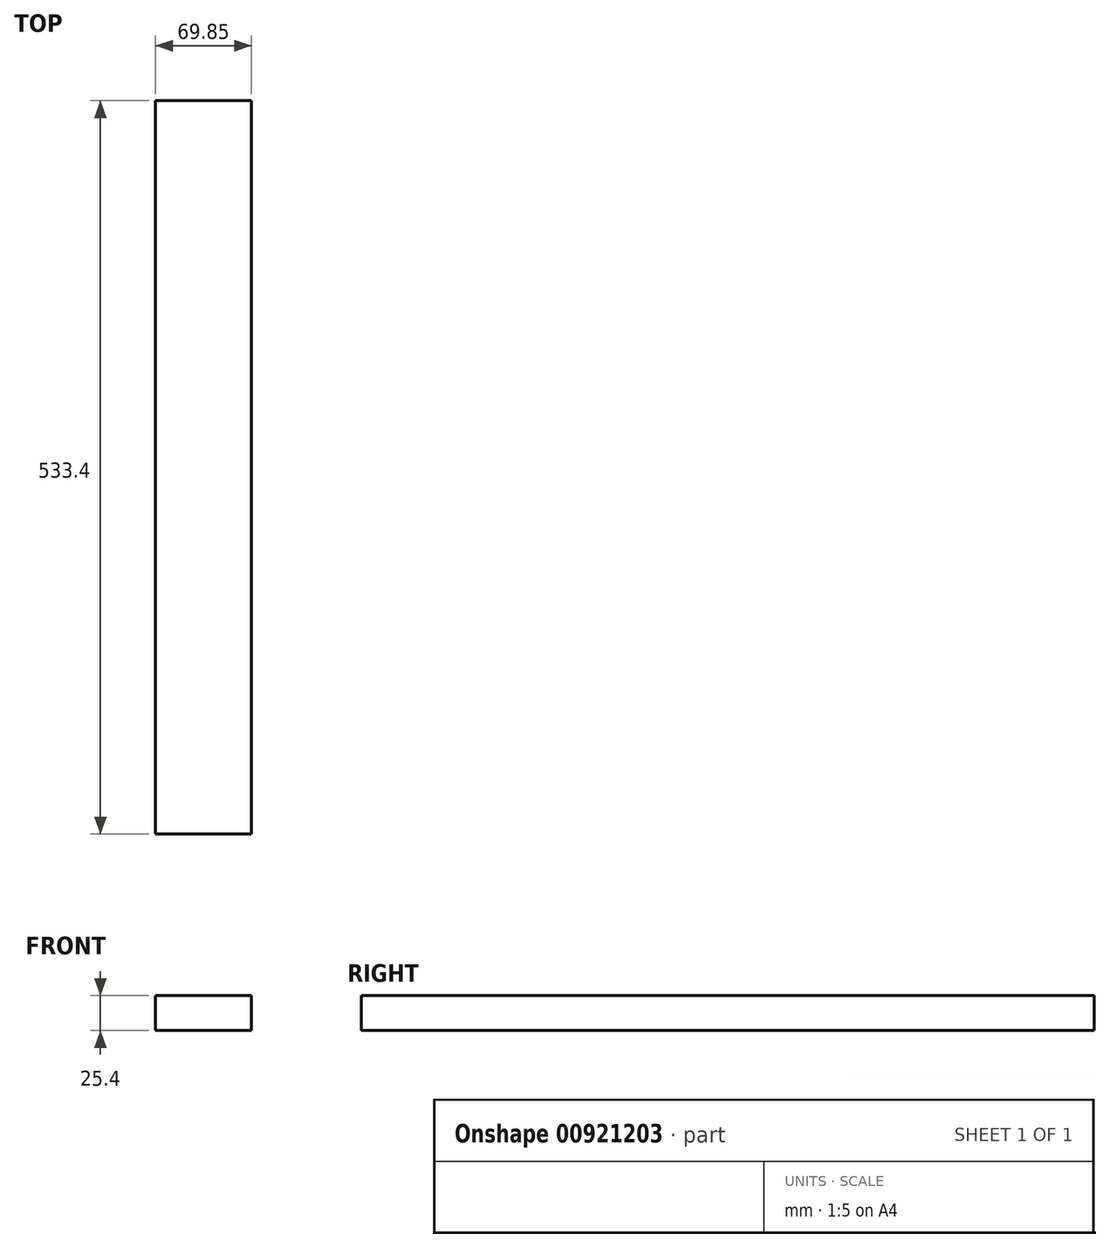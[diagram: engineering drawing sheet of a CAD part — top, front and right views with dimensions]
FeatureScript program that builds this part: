
annotation { "Feature Type Name" : "Feature", "Feature Type Description" : "" }
export const myFeature = defineFeature(function(context is Context, id is Id, definition is map)
    precondition{}
    {
        {
            var Q0;
            Q0=qCreatedBy(makeId("Front.planeOp"),FACE);
            var sketch = newSketch(context, id + "F0", { "sketchPlane" : qUnion([Q0])});
            skLineSegment(sketch, "E0.bottom", {"start": v(0, 0) * mm, "end": v(69.85, 0) * mm});
            skLineSegment(sketch, "E0.top", {"start": v(0, 25.4) * mm, "end": v(69.85, 25.4) * mm});
            skLineSegment(sketch, "E0.left", {"start": v(0, 0) * mm, "end": v(0, 25.4) * mm});
            skLineSegment(sketch, "E0.right", {"start": v(69.85, 0) * mm, "end": v(69.85, 25.4) * mm});
            skSolve(sketch);
        }
        {
            var Q0;
            Q0 = qSketchRegion(id + "F0", true);
            extrude(context, id + "F1", {"entities" : qUnion([Q0]), "depth" : 533.4 * mm, "offsetDistance" : 25.4 * mm});
        }
    });
